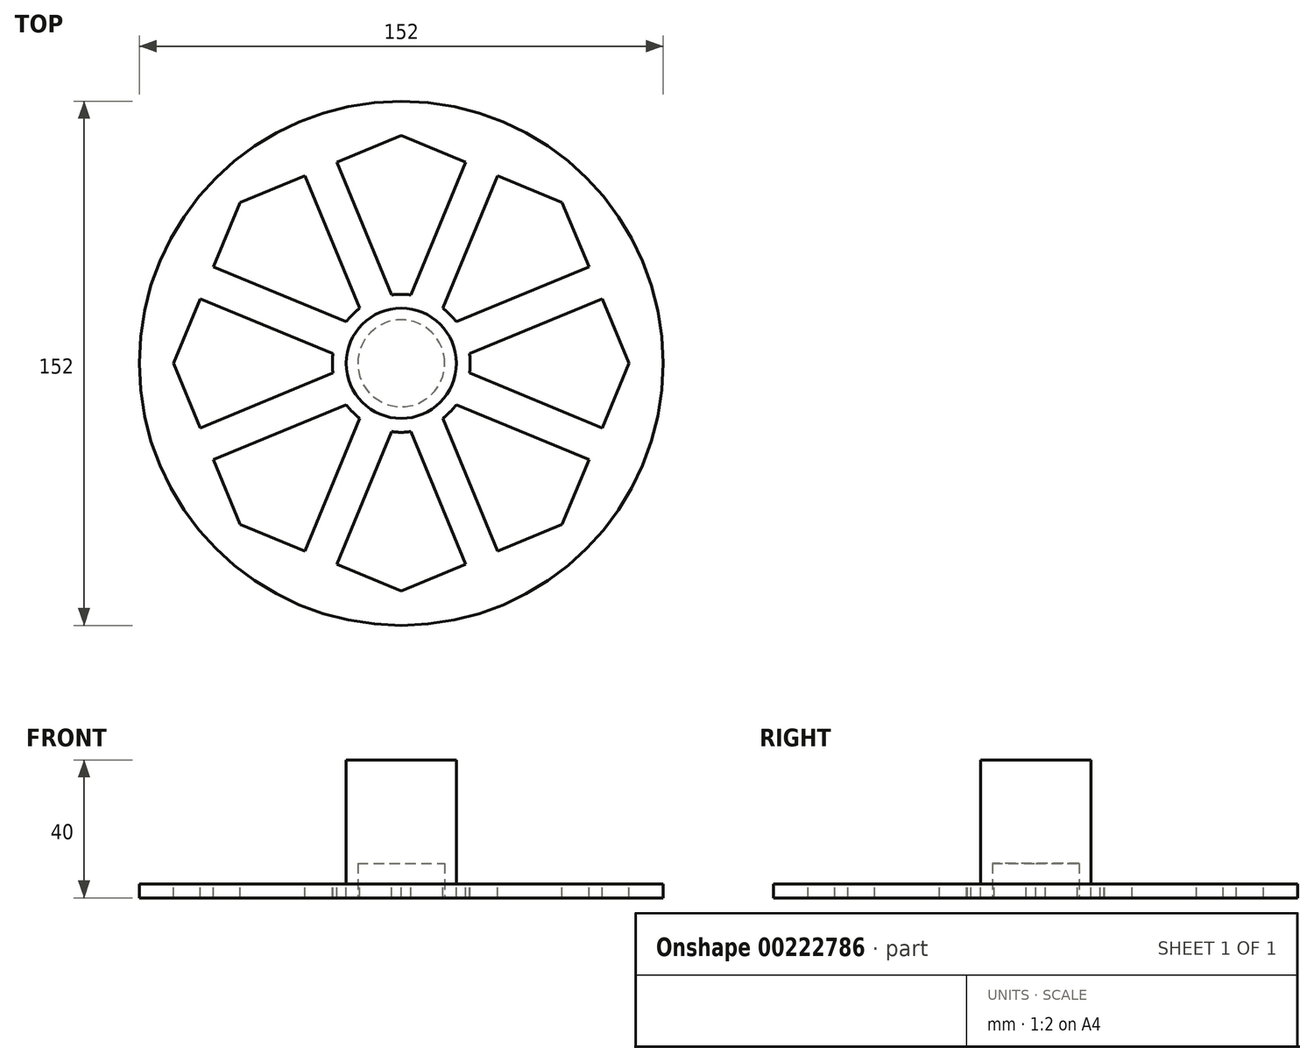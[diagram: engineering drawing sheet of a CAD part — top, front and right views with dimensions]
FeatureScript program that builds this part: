
annotation { "Feature Type Name" : "Feature", "Feature Type Description" : "" }
export const myFeature = defineFeature(function(context is Context, id is Id, definition is map)
    precondition{}
    {
        {
            var Q0;
            Q0=qCreatedBy(makeId("Top.planeOp"),FACE);
            var sketch = newSketch(context, id + "F0", { "sketchPlane" : qUnion([Q0])});
            skCircle(sketch, "E0", {"center": v(0, 0) * mm, "radius": 16 * mm});
            skSolve(sketch);
        }
        {
            var Q0;
            Q0 = qSketchRegion(id + "F0", true);
            extrude(context, id + "F1", {"entities" : qUnion([Q0]), "depth" : 40 * mm});
        }
        {
            var Q0;
            Q0=makeQuery(id+"F1.opExtrude","CAP_FACE",FACE,{"disambiguationData":[OSD([sQuery(id+"F0.wireOp",EDGE,"E0")])],"isStart":true});
            var sketch = newSketch(context, id + "F2", { "sketchPlane" : qUnion([Q0])});
            skCircle(sketch, "E1", {"center": v(0, 0) * mm, "radius": 12.6 * mm});
            skSolve(sketch);
        }
        {
            var Q0;
            Q0 = qSketchRegion(id + "F2", true);
            var Q1;
            Q1=makeQuery(id+"F1.opExtrude","CAP_FACE",FACE,{"disambiguationData":[OSD([sQuery(id+"F0.wireOp",EDGE,"E0")])],"isStart":false});
            extrude(context, id + "F3", {"entities" : qUnion([Q0]), "operationType" : NewBodyOperationType.REMOVE, "oppositeDirection" : true, "endBoundEntityFace" : qUnion([Q1]), "depth" : 10 * mm});
        }
        {
            var Q0;
            Q0=qCreatedBy(makeId("Top.planeOp"),FACE);
            var sketch = newSketch(context, id + "F4", { "sketchPlane" : qUnion([Q0])});
            skCircle(sketch, "E2", {"center": v(0, 0) * mm, "radius": 16 * mm});
            skCircle(sketch, "E3.0", {"center": v(0, 0) * mm, "radius": 76 * mm});
            skSolve(sketch);
        }
        {
            var Q0;
            Q0 = qSketchRegion(id + "F4", true);
            extrude(context, id + "F5", {"entities" : qUnion([Q0]), "operationType" : NewBodyOperationType.ADD, "depth" : 4 * mm});
        }
        {
            var Q0;
            Q0=makeQuery(id+"F5.opExtrude","CAP_FACE",FACE,{"disambiguationData":[OSD([sQuery(id+"F4.wireOp",EDGE,"E2"),sQuery(id+"F4.wireOp",EDGE,"E3.0")])],"isStart":false});
            var sketch = newSketch(context, id + "F6", { "sketchPlane" : qUnion([Q0])});
            skCircle(sketch, "E4.cCircle", {"center": v(0, 0) * mm, "radius": 66 * mm, "construction": true});
            skLineSegment(sketch, "E4.0", {"start": v(46.67, -46.67) * mm, "end": v(27.95, -54.42) * mm});
            skLineSegment(sketch, "E4.1", {"start": v(0, -66) * mm, "end": v(-18.72, -58.25) * mm});
            skLineSegment(sketch, "E4.2", {"start": v(-46.67, -46.67) * mm, "end": v(-54.42, -27.95) * mm});
            skLineSegment(sketch, "E4.3", {"start": v(-66, 0) * mm, "end": v(-58.25, 18.72) * mm});
            skLineSegment(sketch, "E4.4", {"start": v(-46.67, 46.67) * mm, "end": v(-27.95, 54.42) * mm});
            skLineSegment(sketch, "E4.5", {"start": v(0, 66) * mm, "end": v(18.72, 58.25) * mm});
            skLineSegment(sketch, "E4.6", {"start": v(46.67, 46.67) * mm, "end": v(54.42, 27.95) * mm});
            skLineSegment(sketch, "E4.7", {"start": v(66, 0) * mm, "end": v(58.25, -18.72) * mm});
            skArc(sketch, "E5", {"start": v(-15.98, -12.03) * mm, "mid": v(-14.14, -14.14) * mm, "end": v(-12.03, -15.98) * mm});
            skPoint(sketch, "E6", {"position": v(-56.33, 23.33) * mm});
            skPoint(sketch, "E7", {"position": v(-23.33, 56.33) * mm});
            skPoint(sketch, "E8", {"position": v(23.33, 56.33) * mm});
            skPoint(sketch, "E9", {"position": v(56.33, 23.33) * mm});
            skPoint(sketch, "E10", {"position": v(56.33, -23.33) * mm});
            skPoint(sketch, "E11", {"position": v(23.33, -56.33) * mm});
            skPoint(sketch, "E12", {"position": v(-23.33, -56.33) * mm});
            skLineSegment(sketch, "E13", {"start": v(27.95, -54.42) * mm, "end": v(12.03, -15.98) * mm});
            skLineSegment(sketch, "E14", {"start": v(18.72, -58.25) * mm, "end": v(2.8, -19.8) * mm});
            skLineSegment(sketch, "E15.1.0", {"start": v(54.42, -27.95) * mm, "end": v(15.98, -12.03) * mm});
            skLineSegment(sketch, "E15.1.1", {"start": v(58.25, -18.72) * mm, "end": v(19.8, -2.8) * mm});
            skLineSegment(sketch, "E15.2.0", {"start": v(58.25, 18.72) * mm, "end": v(19.8, 2.8) * mm});
            skLineSegment(sketch, "E15.2.1", {"start": v(54.42, 27.95) * mm, "end": v(15.98, 12.03) * mm});
            skLineSegment(sketch, "E15.3.0", {"start": v(27.95, 54.42) * mm, "end": v(12.03, 15.98) * mm});
            skLineSegment(sketch, "E15.3.1", {"start": v(18.72, 58.25) * mm, "end": v(2.8, 19.8) * mm});
            skLineSegment(sketch, "E15.4.0", {"start": v(-18.72, 58.25) * mm, "end": v(-2.8, 19.8) * mm});
            skLineSegment(sketch, "E15.4.1", {"start": v(-27.95, 54.42) * mm, "end": v(-12.03, 15.98) * mm});
            skLineSegment(sketch, "E15.5.0", {"start": v(-54.42, 27.95) * mm, "end": v(-15.98, 12.03) * mm});
            skLineSegment(sketch, "E15.5.1", {"start": v(-58.25, 18.72) * mm, "end": v(-19.8, 2.8) * mm});
            skLineSegment(sketch, "E15.6.0", {"start": v(-58.25, -18.72) * mm, "end": v(-19.8, -2.8) * mm});
            skLineSegment(sketch, "E15.6.1", {"start": v(-54.42, -27.95) * mm, "end": v(-15.98, -12.03) * mm});
            skLineSegment(sketch, "E15.7.0", {"start": v(-27.95, -54.42) * mm, "end": v(-12.03, -15.98) * mm});
            skLineSegment(sketch, "E15.7.1", {"start": v(-18.72, -58.25) * mm, "end": v(-2.8, -19.8) * mm});
            skLineSegment(sketch, "E16.trimOffspring", {"start": v(-58.25, -18.72) * mm, "end": v(-66, 0) * mm});
            skArc(sketch, "E17.trimOffspring", {"start": v(-19.8, 2.8) * mm, "mid": v(-20, 0) * mm, "end": v(-19.8, -2.8) * mm});
            skLineSegment(sketch, "E18.trimOffspring", {"start": v(-54.42, 27.95) * mm, "end": v(-46.67, 46.67) * mm});
            skArc(sketch, "E19.trimOffspring", {"start": v(-2.8, -19.8) * mm, "mid": v(0, -20) * mm, "end": v(2.8, -19.8) * mm});
            skArc(sketch, "E20.trimOffspring", {"start": v(12.03, -15.98) * mm, "mid": v(14.14, -14.14) * mm, "end": v(15.98, -12.03) * mm});
            skArc(sketch, "E21.trimOffspring", {"start": v(-12.03, 15.98) * mm, "mid": v(-14.14, 14.14) * mm, "end": v(-15.98, 12.03) * mm});
            skArc(sketch, "E22.trimOffspring", {"start": v(2.8, 19.8) * mm, "mid": v(0, 20) * mm, "end": v(-2.8, 19.8) * mm});
            skArc(sketch, "E23.trimOffspring", {"start": v(15.98, 12.03) * mm, "mid": v(14.14, 14.14) * mm, "end": v(12.03, 15.98) * mm});
            skArc(sketch, "E24.trimOffspring", {"start": v(19.8, -2.8) * mm, "mid": v(20, 0) * mm, "end": v(19.8, 2.8) * mm});
            skLineSegment(sketch, "E25.trimOffspring", {"start": v(18.72, -58.25) * mm, "end": v(0, -66) * mm});
            skLineSegment(sketch, "E26.trimOffspring", {"start": v(-27.95, -54.42) * mm, "end": v(-46.67, -46.67) * mm});
            skLineSegment(sketch, "E27.trimOffspring", {"start": v(54.42, -27.95) * mm, "end": v(46.67, -46.67) * mm});
            skLineSegment(sketch, "E28.trimOffspring", {"start": v(58.25, 18.72) * mm, "end": v(66, 0) * mm});
            skLineSegment(sketch, "E29.trimOffspring", {"start": v(-18.72, 58.25) * mm, "end": v(0, 66) * mm});
            skLineSegment(sketch, "E30.trimOffspring", {"start": v(27.95, 54.42) * mm, "end": v(46.67, 46.67) * mm});
            skSolve(sketch);
        }
        {
            var Q0;
            Q0 = qSketchRegion(id + "F6", true);
            var Q1;
            Q1=makeQuery(id+"F5.boolean.opBoolean","MERGE",FACE,{"derivedFrom":[makeQuery(id+"F1.opExtrude","CAP_FACE",FACE,{"disambiguationData":[OSD([sQuery(id+"F0.wireOp",EDGE,"E0")])],"isStart":true}),makeQuery(id+"F5.opExtrude","CAP_FACE",FACE,{"disambiguationData":[OSD([sQuery(id+"F4.wireOp",EDGE,"E2"),sQuery(id+"F4.wireOp",EDGE,"E3.0")])],"isStart":true})]});
            extrude(context, id + "F7", {"entities" : qUnion([Q0]), "operationType" : NewBodyOperationType.REMOVE, "endBound" : BoundingType.UP_TO_SURFACE, "oppositeDirection" : true, "endBoundEntityFace" : qUnion([Q1]), "depth" : 25 * mm});
        }
    });
